# Revit family: Access_Door-Hidden_Flange-Cendrex-Removable-RMD
name_source: partatom
category: Specialty Equipment
revit_build: Autodesk Revit Architecture 2013 (Build: 20130531_2115(x64)
units: mm (PartAtom-declared; Revit-internal decimal feet)

## types (5) — shared parameters
Assembly Code = C1020700
Available Options = http://cendrex.com
Cendrex LEED Ready Program = http://www.cendrex.com
Construction Material = Metal - Cendrex - Aluminum
Default Elevation = 0"
Description = Removable aesthetic access door with hidden flange
Finish = Metal - Cendrex - Powder Coated White
Frame Depth = 1 15/32"
Manufacturer = Cendrex
Model = RMD
Product Documentation Link = http://cendrex.com
Product Page URL = http://cendrex.com
URL = http://www.cendrex.com

## per-type parameters (varying)
| type | Door Height | Door Width | Frame Height Calc | Frame Width Calc | Height Actual | Width Actual |
| Custom | 24" | 24" | 24" | 24" | 24" | 24" |
| 8 x 8 | 8" | 8" | 8" | 8" | 8" | 8" |
| 12 x 12 | 12" | 12" | 12" | 12" | 12" | 12" |
| 16 x 16 | 16" | 16" | 16" | 16" | 16" | 16" |
| 24 x 24 | 24" | 24" | 24" | 24" | 24" | 24" |

## geometry (parser evidence)
native form markers: Blend x15, Sweep x6
no freeform markers — native parametric forms only
